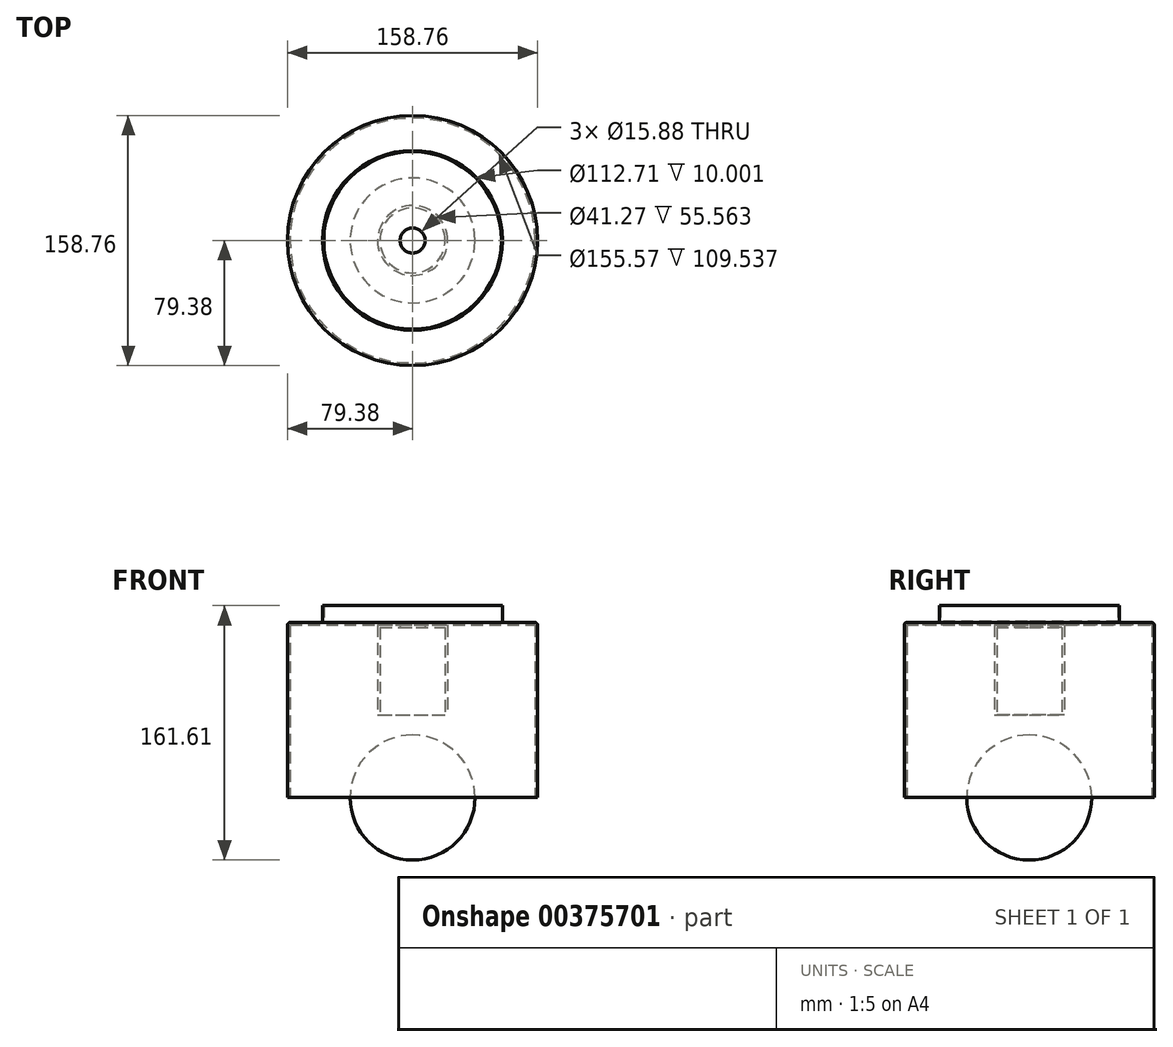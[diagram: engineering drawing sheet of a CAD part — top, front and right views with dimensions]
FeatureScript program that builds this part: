
annotation { "Feature Type Name" : "Feature", "Feature Type Description" : "" }
export const myFeature = defineFeature(function(context is Context, id is Id, definition is map)
    precondition{}
    {
        {
            var Q0;
            Q0=qCreatedBy(makeId("Front.planeOp"),FACE);
            var sketch = newSketch(context, id + "F0", { "sketchPlane" : qUnion([Q0])});
            skLineSegment(sketch, "E0", {"start": v(-77.79, 0) * mm, "end": v(-77.79, 109.54) * mm});
            skLineSegment(sketch, "E1", {"start": v(-77.79, 109.54) * mm, "end": v(-7.94, 109.54) * mm});
            skLineSegment(sketch, "E2", {"start": v(-7.94, 109.54) * mm, "end": v(-7.94, 111.13) * mm});
            skLineSegment(sketch, "E3", {"start": v(-7.94, 111.12) * mm, "end": v(-79.38, 111.12) * mm});
            skLineSegment(sketch, "E4", {"start": v(-79.38, 111.12) * mm, "end": v(-79.38, 0) * mm});
            skLineSegment(sketch, "E5", {"start": v(-79.38, 0) * mm, "end": v(-77.79, 0) * mm});
            skLineSegment(sketch, "E6", {"start": v(-57.15, 121.92) * mm, "end": v(-57.15, 111.13) * mm});
            skLineSegment(sketch, "E7", {"start": v(-57.15, 111.12) * mm, "end": v(-7.94, 111.12) * mm});
            skLineSegment(sketch, "E8", {"start": v(-7.94, 111.13) * mm, "end": v(-7.94, 111.92) * mm});
            skLineSegment(sketch, "E9", {"start": v(-7.94, 111.92) * mm, "end": v(-56.36, 111.92) * mm});
            skLineSegment(sketch, "E10", {"start": v(-56.36, 111.92) * mm, "end": v(-56.36, 121.92) * mm});
            skLineSegment(sketch, "E11", {"start": v(-56.36, 121.92) * mm, "end": v(-57.15, 121.92) * mm});
            skLineSegment(sketch, "E12", {"start": v(-20.64, 107.95) * mm, "end": v(-20.64, 52.39) * mm});
            skLineSegment(sketch, "E13", {"start": v(-22.23, 52.39) * mm, "end": v(-20.64, 52.39) * mm});
            skLineSegment(sketch, "E14", {"start": v(-22.23, 52.39) * mm, "end": v(-22.23, 109.54) * mm});
            skLineSegment(sketch, "E15", {"start": v(0, 0) * mm, "end": v(0, 122.02) * mm, "construction": true});
            skCircle(sketch, "E16", {"center": v(0, 0) * mm, "radius": 39.69 * mm});
            skLineSegment(sketch, "E17", {"start": v(0, 39.69) * mm, "end": v(0, -39.69) * mm});
            skLineSegment(sketch, "E18", {"start": v(-20.64, 107.95) * mm, "end": v(-7.94, 107.95) * mm});
            skLineSegment(sketch, "E19", {"start": v(-7.94, 107.95) * mm, "end": v(-7.94, 109.54) * mm});
            skSolve(sketch);
        }
        {
            var Q0;
            {var subQ0=sQuery(id+"F0.wireOp",EDGE,"E17");Q0=makeQuery(id+"F0.imprint","IMPRINT",FACE,{"disambiguationData":[TD([[makeQuery(id+"F0.imprint","IMPRINT",EDGE,{"derivedFrom":subQ0}),-1.0]])]});}
            var Q1;
            Q1=sQuery(id+"F0.wireOp",EDGE,"E17");
            revolve(context, id + "F1", {"entities" : qUnion([Q0]), "axis" : qUnion([Q1]), "revolveType" : RevolveType.FULL});
        }
        {
            var Q0;
            {var subQ4=sQuery(id+"F0.wireOp",EDGE,"E0");Q0=makeQuery(id+"F0.imprint","IMPRINT",FACE,{"disambiguationData":[TD([[makeQuery(id+"F0.imprint","IMPRINT",EDGE,{"derivedFrom":subQ4}),1.0]])]});}
            var Q1;
            Q1=sQuery(id+"F0.wireOp",EDGE,"E15");
            revolve(context, id + "F2", {"entities" : qUnion([Q0]), "axis" : qUnion([Q1]), "revolveType" : RevolveType.FULL});
        }
        {
            var Q0;
            Q0=makeQuery(id+"F2.opRevolve","SWEPT_EDGE",EDGE,{"disambiguationData":[OSD([sQuery(id+"F0.wireOp",EDGE,"E3"),sQuery(id+"F0.wireOp",EDGE,"E4")])]});
            fillet(context, id + "F3", {"entities" : qUnion([Q0]), "radius" : 1.59 * mm, "tangentPropagation" : true, "allowEdgeOverflow" : false});
        }
        {
            var Q0;
            Q0=makeQuery(id+"F0.imprint","IMPRINT",FACE,{"disambiguationData":[TD([[makeQuery(id+"F0.imprint","IMPRINT",EDGE,{"derivedFrom":sQuery(id+"F0.wireOp",EDGE,"E6")}),1.0]])]});
            var Q1;
            Q1=sQuery(id+"F0.wireOp",EDGE,"E15");
            revolve(context, id + "F4", {"entities" : qUnion([Q0]), "axis" : qUnion([Q1]), "revolveType" : RevolveType.FULL});
        }
        {
            var Q0;
            {var subQ0=sQuery(id+"F0.wireOp",EDGE,"E12");Q0=makeQuery(id+"F0.imprint","IMPRINT",FACE,{"disambiguationData":[TD([[makeQuery(id+"F0.imprint","IMPRINT",EDGE,{"derivedFrom":subQ0}),-1.0]])]});}
            var Q1;
            Q1=sQuery(id+"F0.wireOp",EDGE,"E15");
            revolve(context, id + "F5", {"entities" : qUnion([Q0]), "axis" : qUnion([Q1]), "revolveType" : RevolveType.FULL});
        }
    });
